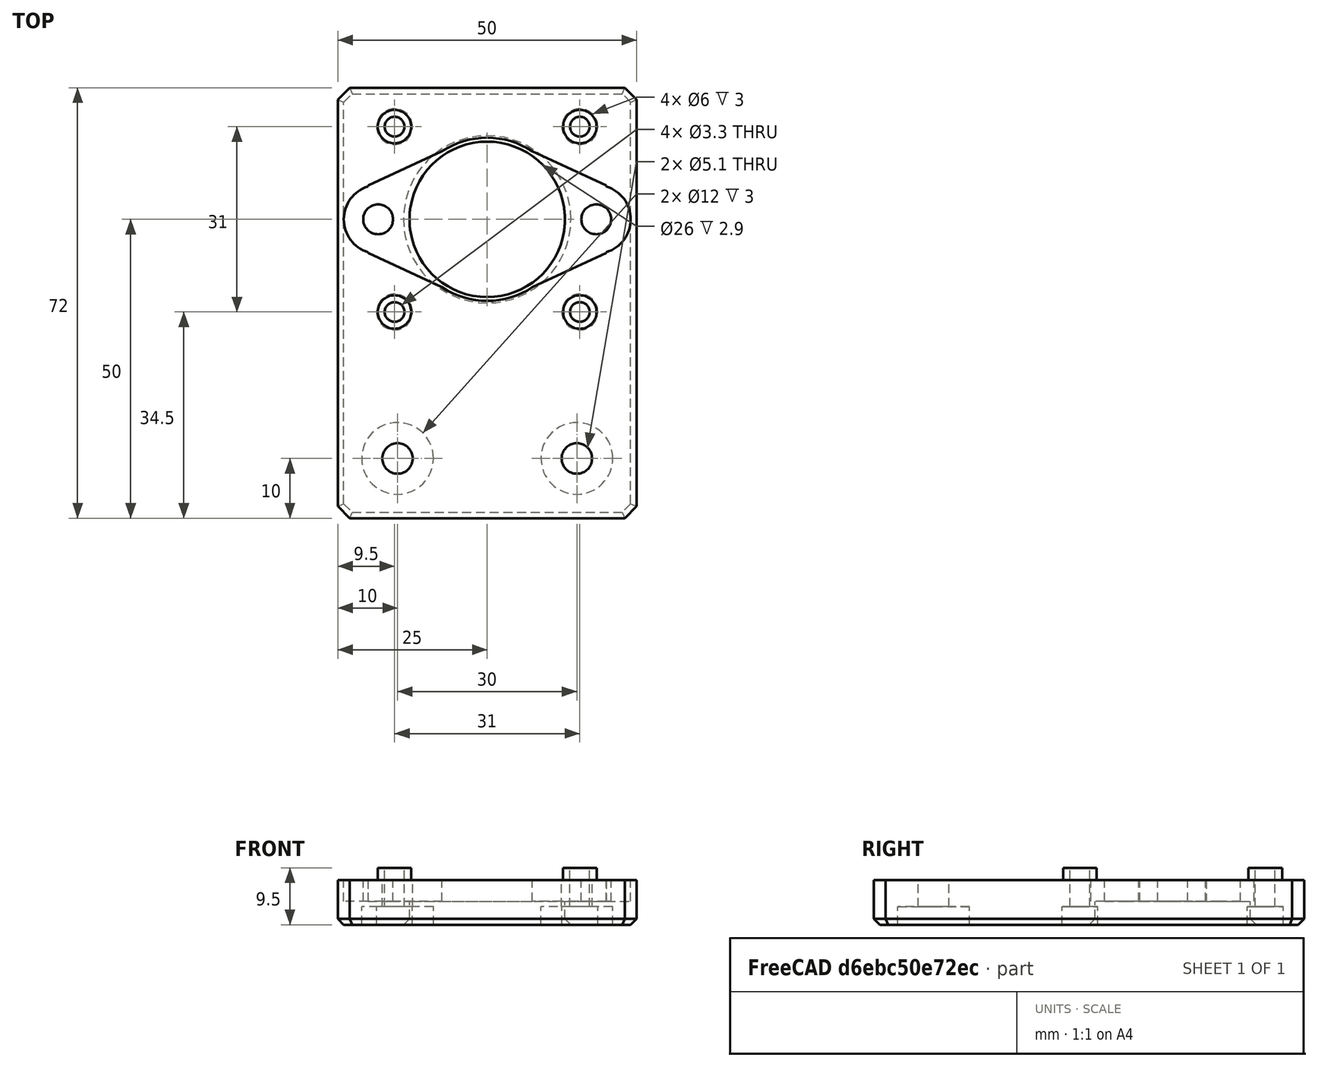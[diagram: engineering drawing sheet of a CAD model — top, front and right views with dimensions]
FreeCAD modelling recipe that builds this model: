
FCSTD DOCUMENT  (FreeCAD 0.18R16146 (Git))
Label: pillow-bearing-mounter
License: All rights reserved
LicenseURL: http://en.wikipedia.org/wiki/All_rights_reserved
objects: Part::Cylinder×23, Part::MultiFuse×8, Part::Cut×6, Part::Box×4, Part::Chamfer×3
note: 44 computed .brp shape members not serialized (recipe doc carries the construction recipe); baked Part::Feature solids carry a one-line shape summary decoded from their .brp

FEATURE [Part::Box] Box  label="Cube"
  AttacherType = Attacher::AttachEngine3D
  Height = 7.5
  Length = 50
  Placement = pos=(-25,-50,0) rot=(0,0,1;0rad)
  Width = 72
FEATURE [Part::Cylinder] Cylinder
  Angle = 360
  AttacherType = Attacher::AttachEngine3D
  Height = 10
  Radius = 13.65
FEATURE [Part::Cylinder] Cylinder001
  Angle = 360
  AttacherType = Attacher::AttachEngine3D
  Height = 6
  Placement = pos=(-18.25,0,4) rot=(0,0,1;0rad)
  Radius = 5.75
FEATURE [Part::Cylinder] Cylinder002
  Angle = 360
  AttacherType = Attacher::AttachEngine3D
  Height = 6
  Placement = pos=(18.25,0,4) rot=(0,0,1;0rad)
  Radius = 5.75
FEATURE [Part::Cylinder] Cylinder003
  Angle = 360
  AttacherType = Attacher::AttachEngine3D
  Height = 7.4
  Placement = pos=(18.25,0,0) rot=(0,0,1;0rad)
  Radius = 2.5
FEATURE [Part::Cylinder] Cylinder004
  Angle = 360
  AttacherType = Attacher::AttachEngine3D
  Height = 7.4
  Placement = pos=(-18.25,0,0) rot=(0,0,1;0rad)
  Radius = 2.5
FEATURE [Part::Cylinder] Cylinder005
  Angle = 360
  AttacherType = Attacher::AttachEngine3D
  Height = 9.5
  Placement = pos=(-15.5,15.5,0) rot=(0,0,1;0rad)
  Radius = 2.8
FEATURE [Part::Cylinder] Cylinder006
  Angle = 360
  AttacherType = Attacher::AttachEngine3D
  Height = 9.5
  Placement = pos=(15.5,15.5,0) rot=(0,0,1;0rad)
  Radius = 2.8
FEATURE [Part::Cylinder] Cylinder007
  Angle = 360
  AttacherType = Attacher::AttachEngine3D
  Height = 9.5
  Placement = pos=(-15.5,-15.5,0) rot=(0,0,1;0rad)
  Radius = 2.8
FEATURE [Part::Cylinder] Cylinder008
  Angle = 360
  AttacherType = Attacher::AttachEngine3D
  Height = 9.5
  Placement = pos=(15.5,-15.5,0) rot=(0,0,1;0rad)
  Radius = 2.8
FEATURE [Part::Cylinder] Cylinder009
  Angle = 360
  AttacherType = Attacher::AttachEngine3D
  Height = 10
  Placement = pos=(15.5,-15.5,0) rot=(0,0,1;0rad)
  Radius = 1.65
FEATURE [Part::Cylinder] Cylinder010
  Angle = 360
  AttacherType = Attacher::AttachEngine3D
  Height = 10
  Placement = pos=(-15.5,-15.5,0) rot=(0,0,1;0rad)
  Radius = 1.65
FEATURE [Part::Cylinder] Cylinder011
  Angle = 360
  AttacherType = Attacher::AttachEngine3D
  Height = 10
  Placement = pos=(15.5,15.5,0) rot=(0,0,1;0rad)
  Radius = 1.65
FEATURE [Part::Cylinder] Cylinder012
  Angle = 360
  AttacherType = Attacher::AttachEngine3D
  Height = 10
  Placement = pos=(-15.5,15.5,0) rot=(0,0,1;0rad)
  Radius = 1.65
FEATURE [Part::Box] Box001  label="Cube001"
  AttacherType = Attacher::AttachEngine3D
  Height = 6
  Length = 48
  Placement = pos=(-24,-5.65,4) rot=(0,0,1;0rad)
  Width = 11.3
FEATURE [Part::MultiFuse] Fusion
  Shapes = -> [Cylinder,Box001]
FEATURE [Part::Chamfer] Chamfer
  Base = -> Fusion
  Edges = 4 edges r=7.5: [Edge16,Edge20,Edge21,Edge23]
FEATURE [Part::Cylinder] Cylinder013
  Angle = 360
  AttacherType = Attacher::AttachEngine3D
  Height = 8
  Placement = pos=(0,0,-1) rot=(0,0,1;0rad)
  Radius = 13
FEATURE [Part::Box] Box002  label="Cube002"
  AttacherType = Attacher::AttachEngine3D
  Height = 10
  Length = 15
  Placement = pos=(19.93,-14,0) rot=(0,0,1;0rad)
  Width = 28
FEATURE [Part::Box] Box003  label="Cube003"
  AttacherType = Attacher::AttachEngine3D
  Height = 10
  Length = 15
  Placement = pos=(-34.93,-14,0) rot=(0,0,1;0rad)
  Width = 28
FEATURE [Part::Cut] Cut
  Base = -> Chamfer
  Tool = -> Box003
FEATURE [Part::Cut] Cut001
  Base = -> Cut
  Tool = -> Box002
FEATURE [Part::Cylinder] Cylinder016
  Angle = 360
  AttacherType = Attacher::AttachEngine3D
  Height = 8
  Placement = pos=(0,0,-4) rot=(0,0,1;0rad)
  Radius = 17
FEATURE [Part::Cut] Cut002
  Base = -> Cut001
  Tool = -> Cylinder016
FEATURE [Part::MultiFuse] Fusion001  label="bearing-template"
  Placement = pos=(0,0,-0.1) rot=(0,0,1;0rad)
  Shapes = -> [Cylinder001,Cut002,Cylinder002]
FEATURE [Part::MultiFuse] Fusion002
  Shapes = -> [Cylinder005,Cylinder007,Cylinder008,Cylinder006]
FEATURE [Part::MultiFuse] Fusion004
  Shapes = -> [Cylinder012,Cylinder010,Cylinder011,Cylinder009]
FEATURE [Part::Cylinder] Cylinder017
  Angle = 360
  AttacherType = Attacher::AttachEngine3D
  Height = 3
  Placement = pos=(-15.5,15.5,0) rot=(0,0,1;0rad)
  Radius = 3
FEATURE [Part::Cylinder] Cylinder018
  Angle = 360
  AttacherType = Attacher::AttachEngine3D
  Height = 3
  Placement = pos=(15.5,15.5,0) rot=(0,0,1;0rad)
  Radius = 3
FEATURE [Part::Cylinder] Cylinder019
  Angle = 360
  AttacherType = Attacher::AttachEngine3D
  Height = 3
  Placement = pos=(15.5,-15.5,0) rot=(0,0,1;0rad)
  Radius = 3
FEATURE [Part::Cylinder] Cylinder020
  Angle = 360
  AttacherType = Attacher::AttachEngine3D
  Height = 3
  Placement = pos=(-15.5,-15.5,0) rot=(0,0,1;0rad)
  Radius = 3
FEATURE [Part::MultiFuse] Fusion005
  Shapes = -> [Cylinder020,Cylinder019,Cylinder018,Cylinder017]
FEATURE [Part::MultiFuse] Fusion007
  Shapes = -> [Cylinder003,Cylinder004]
FEATURE [Part::Cylinder] Cylinder021
  Angle = 360
  AttacherType = Attacher::AttachEngine3D
  Height = 10
  Placement = pos=(-15,-40,0) rot=(0,0,1;0rad)
  Radius = 2.55
FEATURE [Part::Cylinder] Cylinder022
  Angle = 360
  AttacherType = Attacher::AttachEngine3D
  Height = 10
  Placement = pos=(15,-40,0) rot=(0,0,1;0rad)
  Radius = 2.55
FEATURE [Part::Chamfer] Chamfer001
  Base = -> Box
  Edges = 4 edges r=2: [Edge1,Edge3,Edge5,Edge7]
FEATURE [Part::Cut] Cut003
  Base = -> Chamfer001
  Tool = -> Fusion001
FEATURE [Part::Cut] Cut004
  Base = -> Cut003
  Tool = -> Cylinder013
FEATURE [Part::MultiFuse] Fusion008
  Shapes = -> [Cut004,Fusion002,Fusion007]
FEATURE [Part::Cylinder] Cylinder023
  Angle = 360
  AttacherType = Attacher::AttachEngine3D
  Height = 3
  Placement = pos=(15,-40,0) rot=(0,0,1;0rad)
  Radius = 6
FEATURE [Part::Cylinder] Cylinder024
  Angle = 360
  AttacherType = Attacher::AttachEngine3D
  Height = 3
  Placement = pos=(-15,-40,0) rot=(0,0,1;0rad)
  Radius = 6
FEATURE [Part::MultiFuse] Fusion009
  Shapes = -> [Cylinder024,Cylinder023,Cylinder022,Cylinder021,Fusion004,Fusion005]
FEATURE [Part::Cut] Cut005
  Base = -> Fusion008
  Tool = -> Fusion009
FEATURE [Part::Chamfer] Chamfer002
  Base = -> Cut005
  Edges = 9 edges r=1: [Edge4,Edge35,Edge37,Edge39,Edge40,Edge41,Edge42,Edge43,Edge44]
